# Revit family: Specialty Equipment_Grab Rail_Metlam_MLR 112-AL
name_source: partatom
category: Specialty Equipment
revit_build: Autodesk Revit 2014 (Build: 20130308_1515(x64)
units: mm (PartAtom-declared; Revit-internal decimal feet)

## types (1)
- 450w x 450h x 90d
    Assembly Code = C1030200
    Description = 90° Ambulant Anti- Ligature Grab Rail
    Grab Rail Material = z_Metlam_Stainless Steel
    Manufacturer = Metlam
    Manufacturer_Overall Depth = 90 mm  [stored 0.295276 ft]
    Manufacturer_Overall Height = 450 mm  [stored 1.47638 ft]
    Manufacturer_Overall Width = 450 mm  [stored 1.47638 ft]
    Manufacturer_Spec Code = MLR 112-AL
    Manufacturer_URL_Home Page = http://www.metlam.com.au
    Manufacturer_URL__Product Specific = http://metlam.com.au
    Model = MLR 112-AL
    ModifiedIssue_ANZRS = 20151029 $
    Type Comments = Grab Rails
    URL = http://www.metlam.com.au

note: [stored X ft] marks values corroborated as IEEE doubles in the binary element streams (Revit-internal decimal feet)

## geometry (parser evidence)
native form markers: Sweep x3
no freeform markers — native parametric forms only
